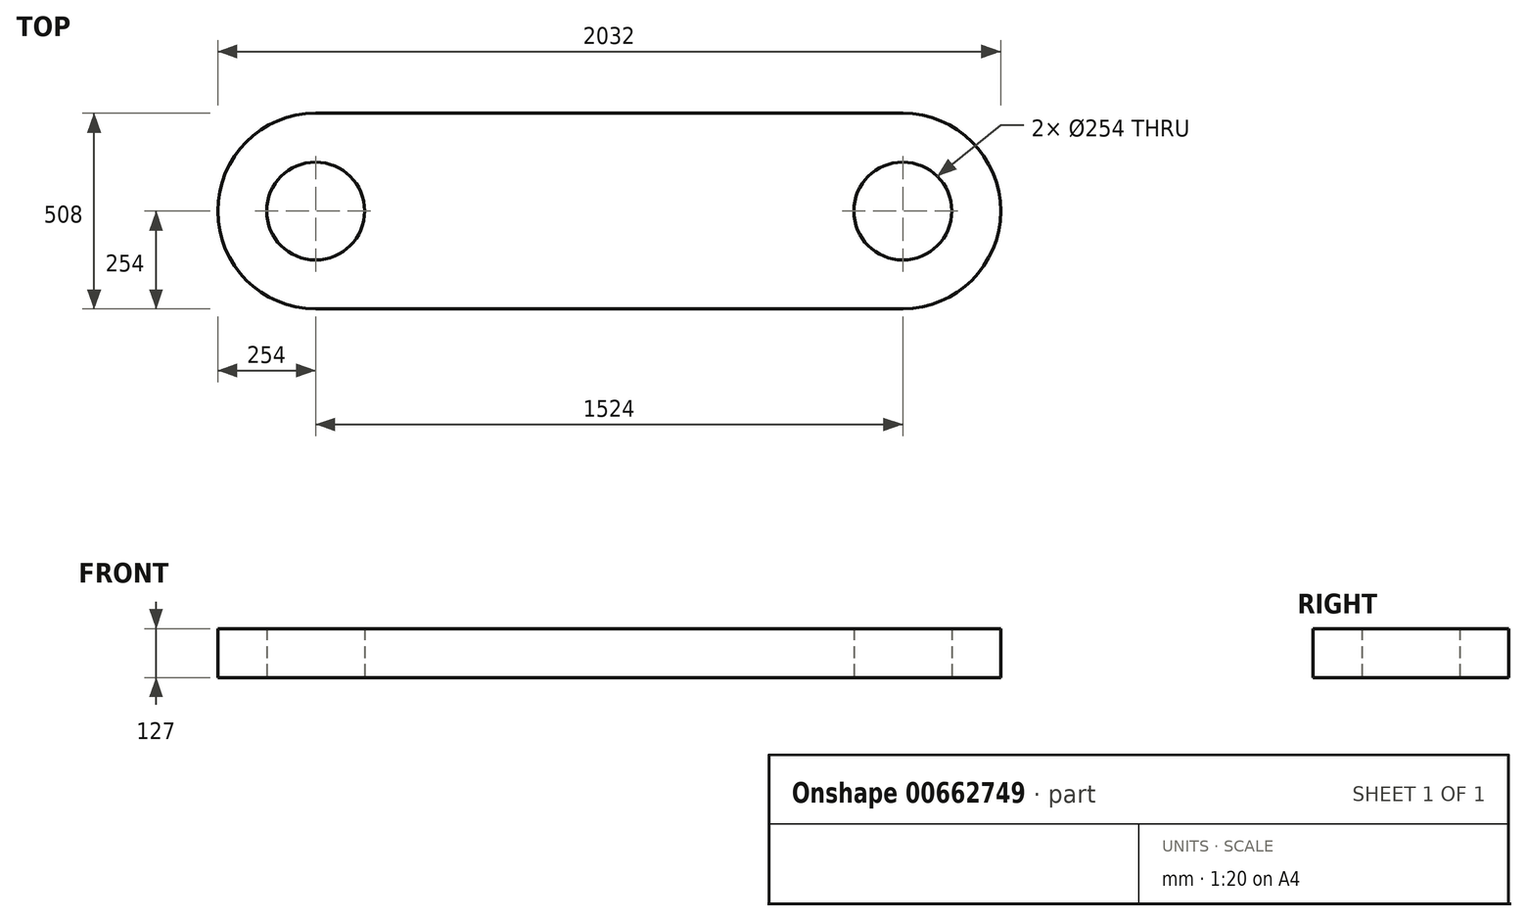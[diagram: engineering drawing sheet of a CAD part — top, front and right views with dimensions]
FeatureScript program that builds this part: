
annotation { "Feature Type Name" : "Feature", "Feature Type Description" : "" }
export const myFeature = defineFeature(function(context is Context, id is Id, definition is map)
    precondition{}
    {
        {
            var Q0;
            Q0=qCreatedBy(makeId("Top.planeOp"),FACE);
            var sketch = newSketch(context, id + "F0", { "sketchPlane" : qUnion([Q0])});
            skLineSegment(sketch, "E0.bottom", {"start": v(-762, 254) * mm, "end": v(762, 254) * mm});
            skLineSegment(sketch, "E0.top", {"start": v(-762, -254) * mm, "end": v(762, -254) * mm});
            skLineSegment(sketch, "E0.left", {"start": v(-762, 254) * mm, "end": v(-762, -254) * mm, "construction": true});
            skLineSegment(sketch, "E0.right", {"start": v(762, 254) * mm, "end": v(762, -254) * mm, "construction": true});
            skArc(sketch, "E1", {"start": v(-762, 254) * mm, "mid": v(-1016, 0) * mm, "end": v(-762, -254) * mm});
            skArc(sketch, "E2", {"start": v(762, -254) * mm, "mid": v(1016, 0) * mm, "end": v(762, 254) * mm});
            skCircle(sketch, "E3", {"center": v(762, 0) * mm, "radius": 127 * mm});
            skCircle(sketch, "E4", {"center": v(-762, 0) * mm, "radius": 127 * mm});
            skSolve(sketch);
        }
        {
            var Q0;
            Q0 = qSketchRegion(id + "F0", true);
            extrude(context, id + "F1", {"entities" : qUnion([Q0]), "depth" : 127 * mm, "offsetDistance" : 25.4 * mm});
        }
    });
